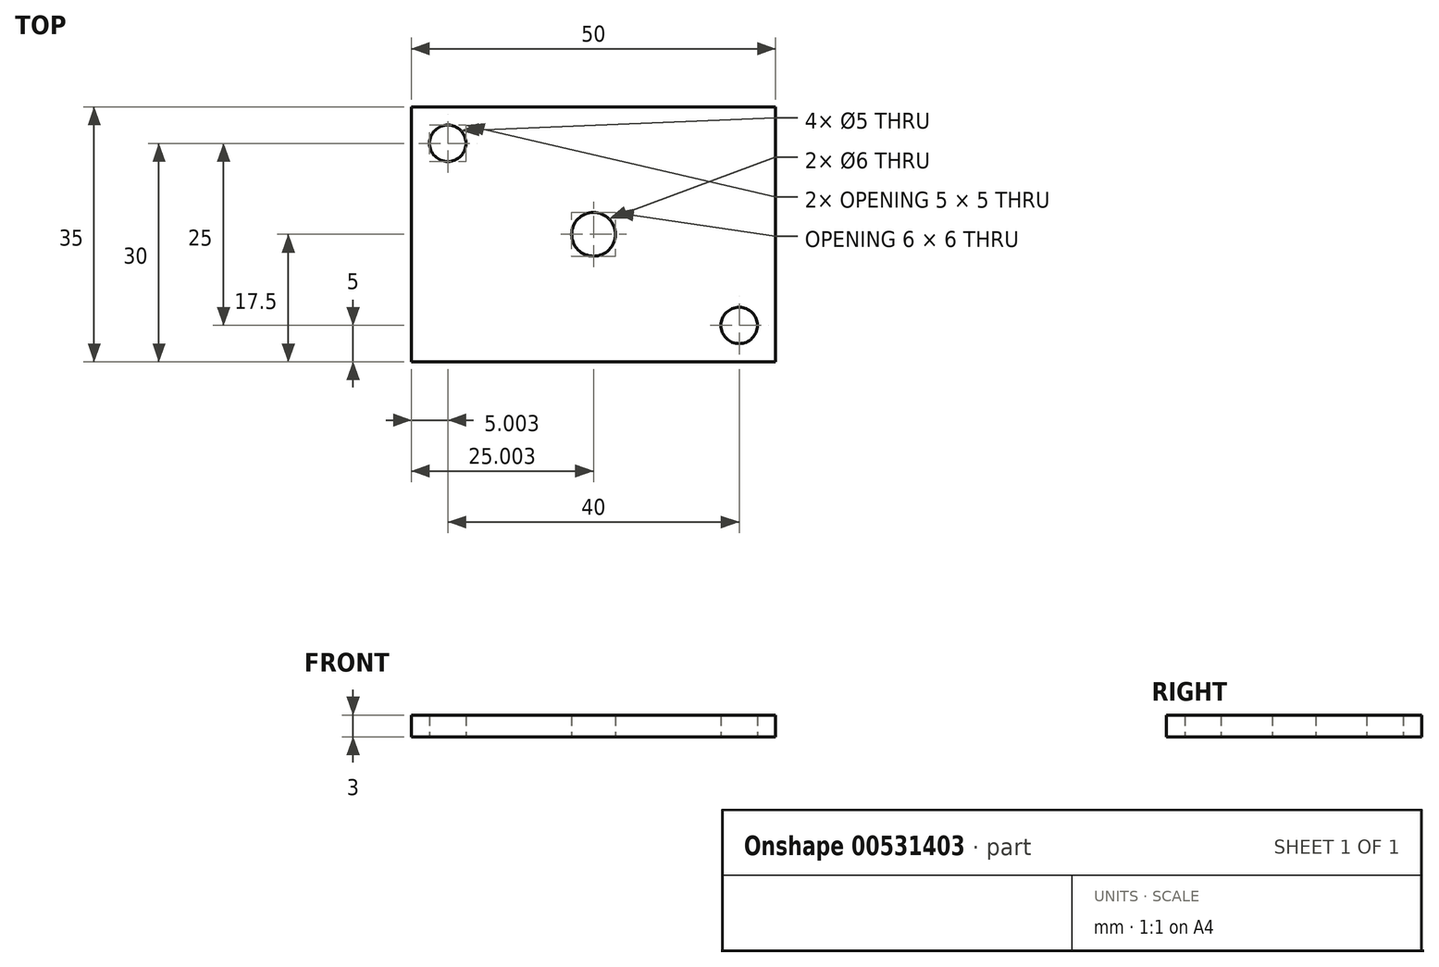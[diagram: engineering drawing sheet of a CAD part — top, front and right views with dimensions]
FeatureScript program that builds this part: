
annotation { "Feature Type Name" : "Feature", "Feature Type Description" : "" }
export const myFeature = defineFeature(function(context is Context, id is Id, definition is map)
    precondition{}
    {
        {
            var Q0;
            Q0=qCreatedBy(makeId("Top.planeOp"),FACE);
            var sketch = newSketch(context, id + "F0", { "sketchPlane" : qUnion([Q0])});
            skLineSegment(sketch, "E0.bottom", {"start": v(-47.2, 48.44) * mm, "end": v(2.8, 48.44) * mm});
            skLineSegment(sketch, "E0.top", {"start": v(-47.2, 13.44) * mm, "end": v(2.8, 13.44) * mm});
            skLineSegment(sketch, "E0.left", {"start": v(-47.2, 48.44) * mm, "end": v(-47.2, 13.44) * mm});
            skLineSegment(sketch, "E0.right", {"start": v(2.8, 48.44) * mm, "end": v(2.8, 13.44) * mm});
            skPoint(sketch, "E0.middle", {"position": v(-22.2, 30.94) * mm});
            skPoint(sketch, "E1", {"position": v(-42.2, 43.44) * mm});
            skPoint(sketch, "E2", {"position": v(-2.2, 18.44) * mm});
            skSolve(sketch);
        }
        {
            var Q0;
            Q0 = qSketchRegion(id + "F0", true);
            extrude(context, id + "F1", {"entities" : qUnion([Q0]), "depth" : 3 * mm, "offsetDistance" : 25 * mm});
        }
        {
            var Q0;
            Q0=sQuery(id+"F0.wireOp",VERTEX,"E0.middle");
            var Q1;
            Q1=makeQuery(id+"F1.opExtrude","SWEPT_BODY",BODY,{"disambiguationData":[OSD([sQuery(id+"F0.wireOp",EDGE,"E0.bottom"),sQuery(id+"F0.wireOp",EDGE,"E0.top"),sQuery(id+"F0.wireOp",EDGE,"E0.left"),sQuery(id+"F0.wireOp",EDGE,"E0.right")])]});
            hole(context, id + "F2", {"style" : HoleStyle.SIMPLE, "endStyle" : HoleEndStyle.THROUGH, "oppositeDirection" : true, "holeDiameter" : 6 * mm, "isTappedThrough" : true, "tappedDepth" : 12 * mm, "tapClearance" : 3, "locations" : qUnion([Q0]), "scope" : qUnion([Q1])});
        }
        {
            var Q0;
            Q0=sQuery(id+"F0.wireOp",VERTEX,"E2");
            var Q1;
            Q1=makeQuery(id+"F1.opExtrude","SWEPT_BODY",BODY,{"disambiguationData":[OSD([sQuery(id+"F0.wireOp",EDGE,"E0.bottom"),sQuery(id+"F0.wireOp",EDGE,"E0.top"),sQuery(id+"F0.wireOp",EDGE,"E0.left"),sQuery(id+"F0.wireOp",EDGE,"E0.right")])]});
            hole(context, id + "F3", {"style" : HoleStyle.SIMPLE, "endStyle" : HoleEndStyle.THROUGH, "oppositeDirection" : true, "holeDiameter" : 5 * mm, "isTappedThrough" : true, "tappedDepth" : 12 * mm, "tapClearance" : 3, "locations" : qUnion([Q0]), "scope" : qUnion([Q1])});
        }
        {
            var Q0;
            Q0=sQuery(id+"F0.wireOp",VERTEX,"E1");
            var Q1;
            Q1=makeQuery(id+"F1.opExtrude","SWEPT_BODY",BODY,{"disambiguationData":[OSD([sQuery(id+"F0.wireOp",EDGE,"E0.bottom"),sQuery(id+"F0.wireOp",EDGE,"E0.top"),sQuery(id+"F0.wireOp",EDGE,"E0.left"),sQuery(id+"F0.wireOp",EDGE,"E0.right")])]});
            hole(context, id + "F4", {"style" : HoleStyle.SIMPLE, "endStyle" : HoleEndStyle.THROUGH, "oppositeDirection" : true, "holeDiameter" : 5 * mm, "isTappedThrough" : true, "tappedDepth" : 12 * mm, "tapClearance" : 3, "locations" : qUnion([Q0]), "scope" : qUnion([Q1])});
        }
    });
